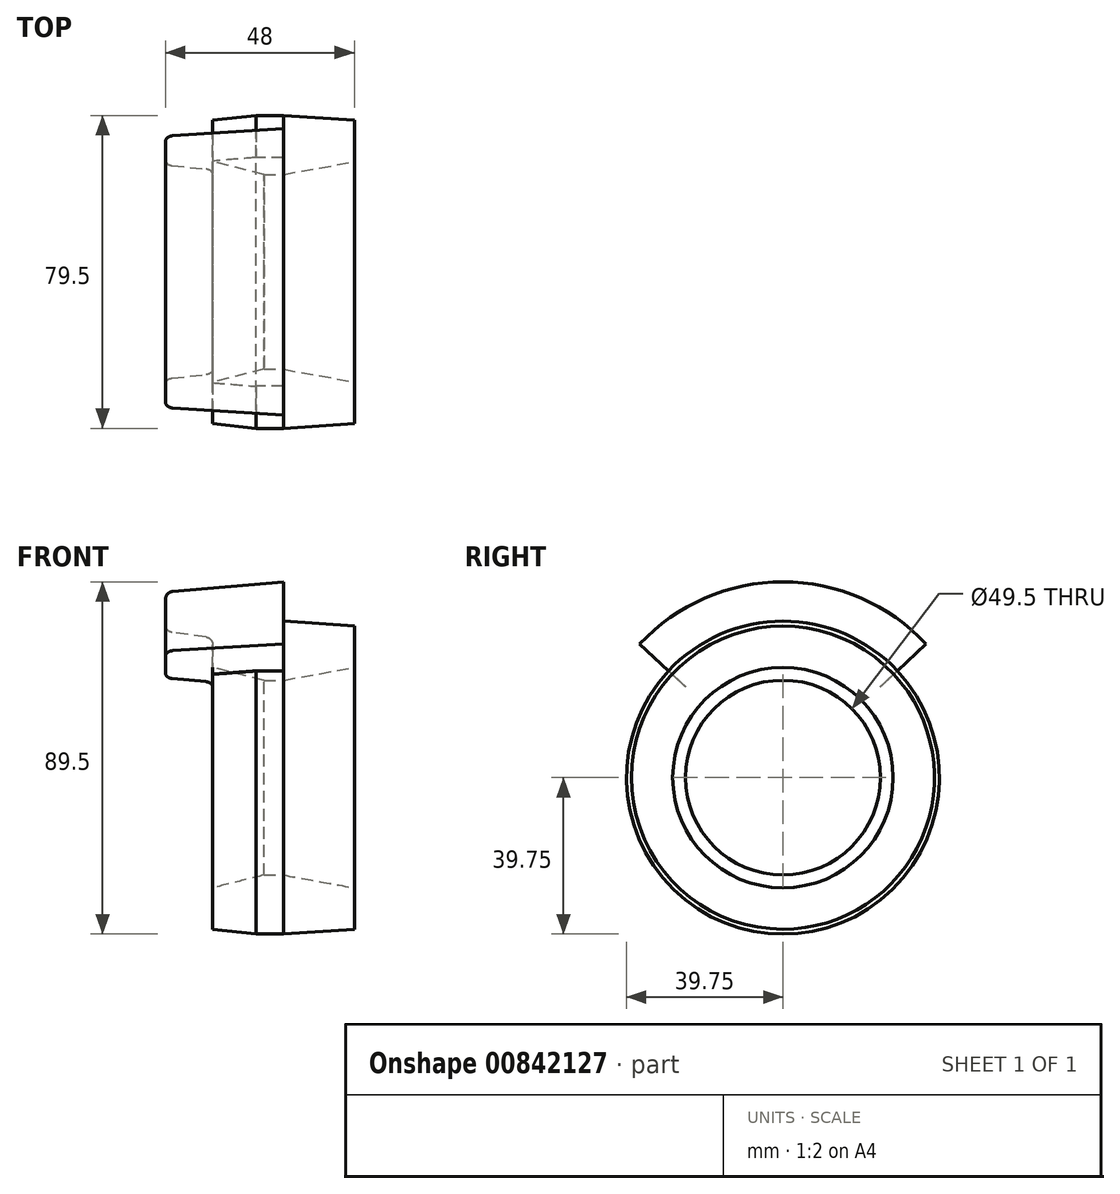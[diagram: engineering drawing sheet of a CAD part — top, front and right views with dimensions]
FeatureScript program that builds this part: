
annotation { "Feature Type Name" : "Feature", "Feature Type Description" : "" }
export const myFeature = defineFeature(function(context is Context, id is Id, definition is map)
    precondition{}
    {
        {
            var Q0;
            Q0=qCreatedBy(makeId("Front.planeOp"),FACE);
            var sketch = newSketch(context, id + "F0", { "sketchPlane" : qUnion([Q0])});
            skLineSegment(sketch, "E0", {"start": v(0, 24.75) * mm, "end": v(0, 39.75) * mm});
            skLineSegment(sketch, "E1", {"start": v(0, 39.75) * mm, "end": v(-7, 39.75) * mm});
            skLineSegment(sketch, "E2", {"start": v(0, 39.75) * mm, "end": v(0, 24.75) * mm});
            skLineSegment(sketch, "E3", {"start": v(-5, 24.75) * mm, "end": v(0, 24.75) * mm});
            skLineSegment(sketch, "E4", {"start": v(0, 0) * mm, "end": v(18, 0) * mm});
            skLineSegment(sketch, "E5", {"start": v(18, 28) * mm, "end": v(18, 38.5) * mm});
            skLineSegment(sketch, "E6", {"start": v(0, 0) * mm, "end": v(-18, 0) * mm});
            skLineSegment(sketch, "E7", {"start": v(-18, 28) * mm, "end": v(-18, 38.5) * mm});
            skLineSegment(sketch, "E8", {"start": v(0, 24.75) * mm, "end": v(18, 28) * mm});
            skLineSegment(sketch, "E9", {"start": v(-5, 24.75) * mm, "end": v(-18, 28) * mm});
            skLineSegment(sketch, "E10", {"start": v(-18, 38.5) * mm, "end": v(-7, 39.75) * mm});
            skLineSegment(sketch, "E11", {"start": v(0, 39.75) * mm, "end": v(18, 38.5) * mm});
            skSolve(sketch);
        }
        {
            var Q0;
            Q0 = qSketchRegion(id + "F0", true);
            var Q1;
            Q1=sQuery(id+"F0.wireOp",EDGE,"E6");
            revolve(context, id + "F1", {"surfaceOperationType" : NewSurfaceOperationType.NEW, "entities" : qUnion([Q0]), "axis" : qUnion([Q1]), "revolveType" : RevolveType.FULL});
        }
        {
            var Q0;
            Q0=qCreatedBy(makeId("Front.planeOp"),FACE);
            var sketch = newSketch(context, id + "F2", { "sketchPlane" : qUnion([Q0])});
            skLineSegment(sketch, "E12", {"start": v(0, 0) * mm, "end": v(0, 39.75) * mm});
            skLineSegment(sketch, "E13", {"start": v(0, 39.75) * mm, "end": v(0, 49.75) * mm});
            skLineSegment(sketch, "E14", {"start": v(-30, 45.3) * mm, "end": v(-30, 38.87) * mm});
            skLineSegment(sketch, "E15", {"start": v(0, 0) * mm, "end": v(-18, 0) * mm});
            skLineSegment(sketch, "E16", {"start": v(-18, 0) * mm, "end": v(-18, 28) * mm});
            skLineSegment(sketch, "E17", {"start": v(0, 49.75) * mm, "end": v(-28.17, 47.29) * mm});
            skLineSegment(sketch, "E18", {"start": v(-28.27, 36.9) * mm, "end": v(-20.27, 35.8) * mm});
            skLineSegment(sketch, "E19", {"start": v(0, 39.75) * mm, "end": v(-7, 39.75) * mm});
            skLineSegment(sketch, "E20", {"start": v(-18, 37.79) * mm, "end": v(-18, 38.5) * mm});
            skLineSegment(sketch, "E21", {"start": v(-18, 38.5) * mm, "end": v(-7, 39.75) * mm});
            skArc(sketch, "E22.filletArc", {"start": v(-28.17, 47.29) * mm, "mid": v(-29.47, 46.64) * mm, "end": v(-30, 45.3) * mm});
            skArc(sketch, "E23.filletArc", {"start": v(-30, 38.87) * mm, "mid": v(-29.5, 37.56) * mm, "end": v(-28.27, 36.9) * mm});
            skPoint(sketch, "E24.visualSharp", {"position": v(-18, 35.5) * mm});
            skLineSegment(sketch, "E25", {"start": v(-20.27, 35.8) * mm, "end": v(-19.73, 35.73) * mm});
            skArc(sketch, "E26.filletArc", {"start": v(-18, 33.75) * mm, "mid": v(-18.5, 35.07) * mm, "end": v(-19.73, 35.73) * mm});
            skLineSegment(sketch, "E27", {"start": v(-18, 33.75) * mm, "end": v(-18, 37.79) * mm});
            skSolve(sketch);
        }
        {
            var Q0;
            Q0=makeQuery(id+"F2.imprint","IMPRINT",FACE,{"disambiguationData":[TD([[makeQuery(id+"F2.imprint","IMPRINT",EDGE,{"derivedFrom":sQuery(id+"F2.wireOp",EDGE,"E13")}),1.0]])]});
            var Q1;
            Q1=makeQuery(id+"F1.opRevolve","SWEPT_EDGE",EDGE,{"disambiguationData":[OSD([sQuery(id+"F0.wireOp",EDGE,"E7"),sQuery(id+"F0.wireOp",EDGE,"E9")])]});
            revolve(context, id + "F3", {"operationType" : NewBodyOperationType.ADD, "surfaceOperationType" : NewSurfaceOperationType.NEW, "entities" : qUnion([Q0]), "axis" : qUnion([Q1]), "revolveType" : RevolveType.TWO_DIRECTIONS, "oppositeDirection" : true, "angle" : 47 * degree, "angleBack" : 313 * degree});
        }
    });
